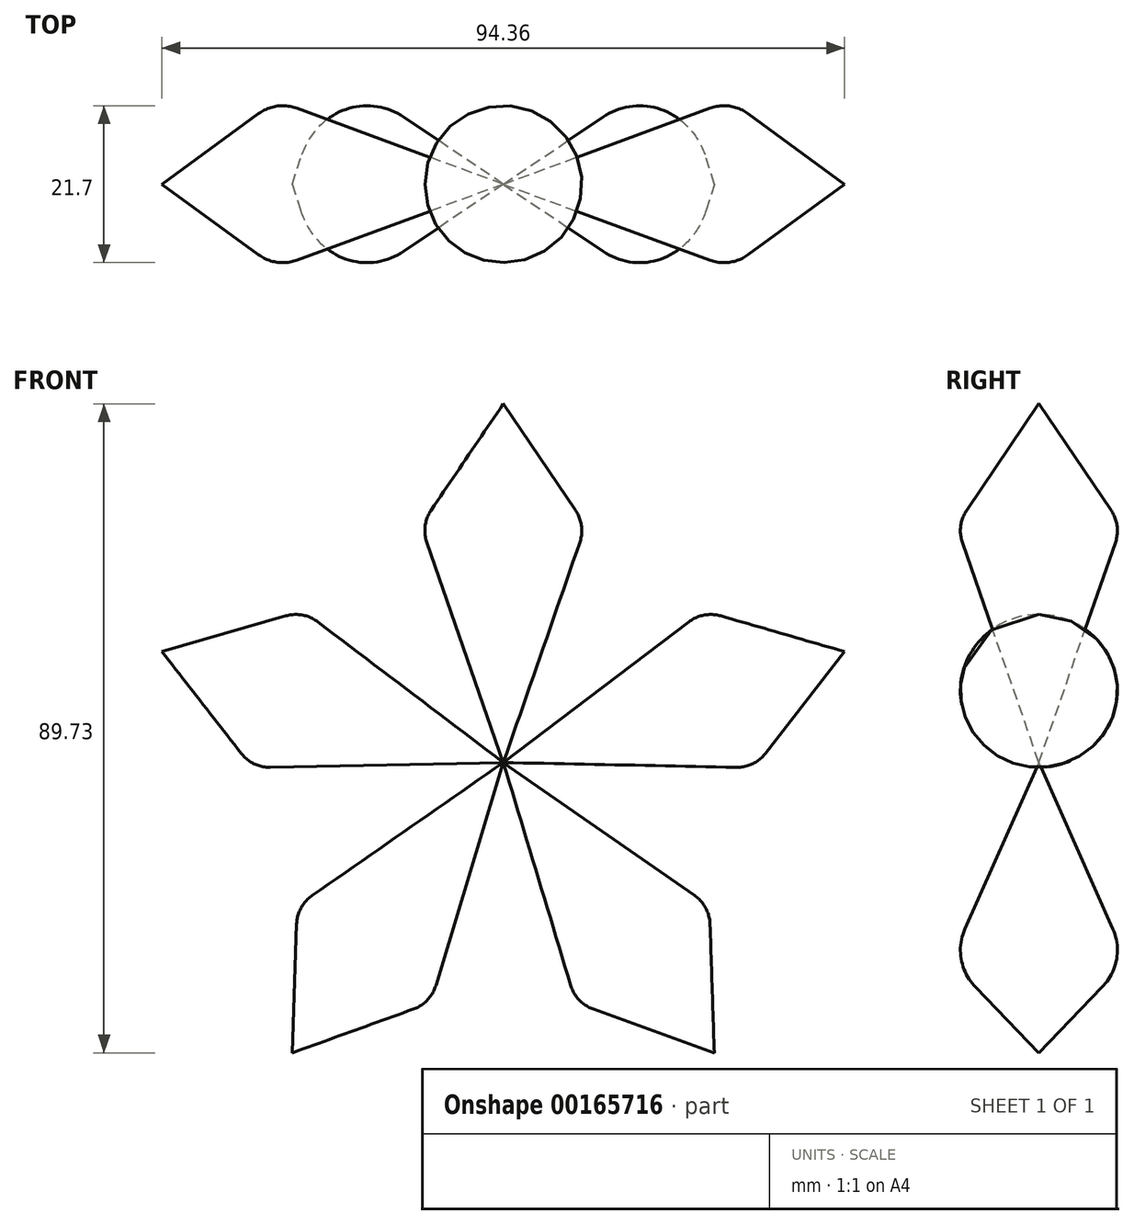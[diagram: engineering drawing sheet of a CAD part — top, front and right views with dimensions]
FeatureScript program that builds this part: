
annotation { "Feature Type Name" : "Feature", "Feature Type Description" : "" }
export const myFeature = defineFeature(function(context is Context, id is Id, definition is map)
    precondition{}
    {
        {
            var Q0;
            Q0=qCreatedBy(makeId("Front.planeOp"),FACE);
            var sketch = newSketch(context, id + "F0", { "sketchPlane" : qUnion([Q0])});
            skLineSegment(sketch, "E0", {"start": v(0, 0) * mm, "end": v(-11.4, 32.79) * mm});
            skLineSegment(sketch, "E1", {"start": v(-11.4, 32.79) * mm, "end": v(0, 49.6) * mm});
            skLineSegment(sketch, "E2", {"start": v(0, 49.6) * mm, "end": v(0, 0) * mm});
            skCircle(sketch, "E3", {"center": v(0, 0) * mm, "radius": 2.81 * mm, "construction": true});
            skSolve(sketch);
        }
        {
            var Q0;
            Q0 = qSketchRegion(id + "F0", true);
            var Q1;
            Q1=sQuery(id+"F0.wireOp",EDGE,"E2");
            revolve(context, id + "F1", {"entities" : qUnion([Q0]), "axis" : qUnion([Q1]), "revolveType" : RevolveType.FULL});
        }
        {
            var Q0;
            Q0=makeQuery(id+"F1.opRevolve","SWEPT_BODY",BODY,{"disambiguationData":[OSD([sQuery(id+"F0.wireOp",EDGE,"E0"),sQuery(id+"F0.wireOp",EDGE,"E1"),sQuery(id+"F0.wireOp",EDGE,"E2")])]});
            var Q1;
            Q1=sQuery(id+"F0.wireOp",EDGE,"E3");
            circularPattern(context, id + "F2", {"entities" : qUnion([Q0]), "axis" : qUnion([Q1]), "angle" : 360 * degree, "instanceCount" : 5, "equalSpace" : true});
        }
        {
            var Q0;
            Q0=makeQuery(id+"F2.opPattern","COPY",EDGE,{"derivedFrom":makeQuery(id+"F1.opRevolve","SWEPT_EDGE",EDGE,{"disambiguationData":[OSD([sQuery(id+"F0.wireOp",EDGE,"E0"),sQuery(id+"F0.wireOp",EDGE,"E1")])]}),"instanceName":"4"});
            var Q1;
            Q1=makeQuery(id+"F2.opPattern","COPY",EDGE,{"derivedFrom":makeQuery(id+"F1.opRevolve","SWEPT_EDGE",EDGE,{"disambiguationData":[OSD([sQuery(id+"F0.wireOp",EDGE,"E0"),sQuery(id+"F0.wireOp",EDGE,"E1")])]}),"instanceName":"3"});
            var Q2;
            Q2=makeQuery(id+"F2.opPattern","COPY",EDGE,{"derivedFrom":makeQuery(id+"F1.opRevolve","SWEPT_EDGE",EDGE,{"disambiguationData":[OSD([sQuery(id+"F0.wireOp",EDGE,"E0"),sQuery(id+"F0.wireOp",EDGE,"E1")])]}),"instanceName":"2"});
            var Q3;
            Q3=makeQuery(id+"F2.opPattern","COPY",EDGE,{"derivedFrom":makeQuery(id+"F1.opRevolve","SWEPT_EDGE",EDGE,{"disambiguationData":[OSD([sQuery(id+"F0.wireOp",EDGE,"E0"),sQuery(id+"F0.wireOp",EDGE,"E1")])]}),"instanceName":"1"});
            var Q4;
            Q4=makeQuery(id+"F1.opRevolve","SWEPT_EDGE",EDGE,{"disambiguationData":[OSD([sQuery(id+"F0.wireOp",EDGE,"E0"),sQuery(id+"F0.wireOp",EDGE,"E1")])]});
            fillet(context, id + "F3", {"entities" : qUnion([Q0, Q1, Q2, Q3, Q4]), "radius" : 5 * mm, "tangentPropagation" : true, "allowEdgeOverflow" : false});
        }
    });
